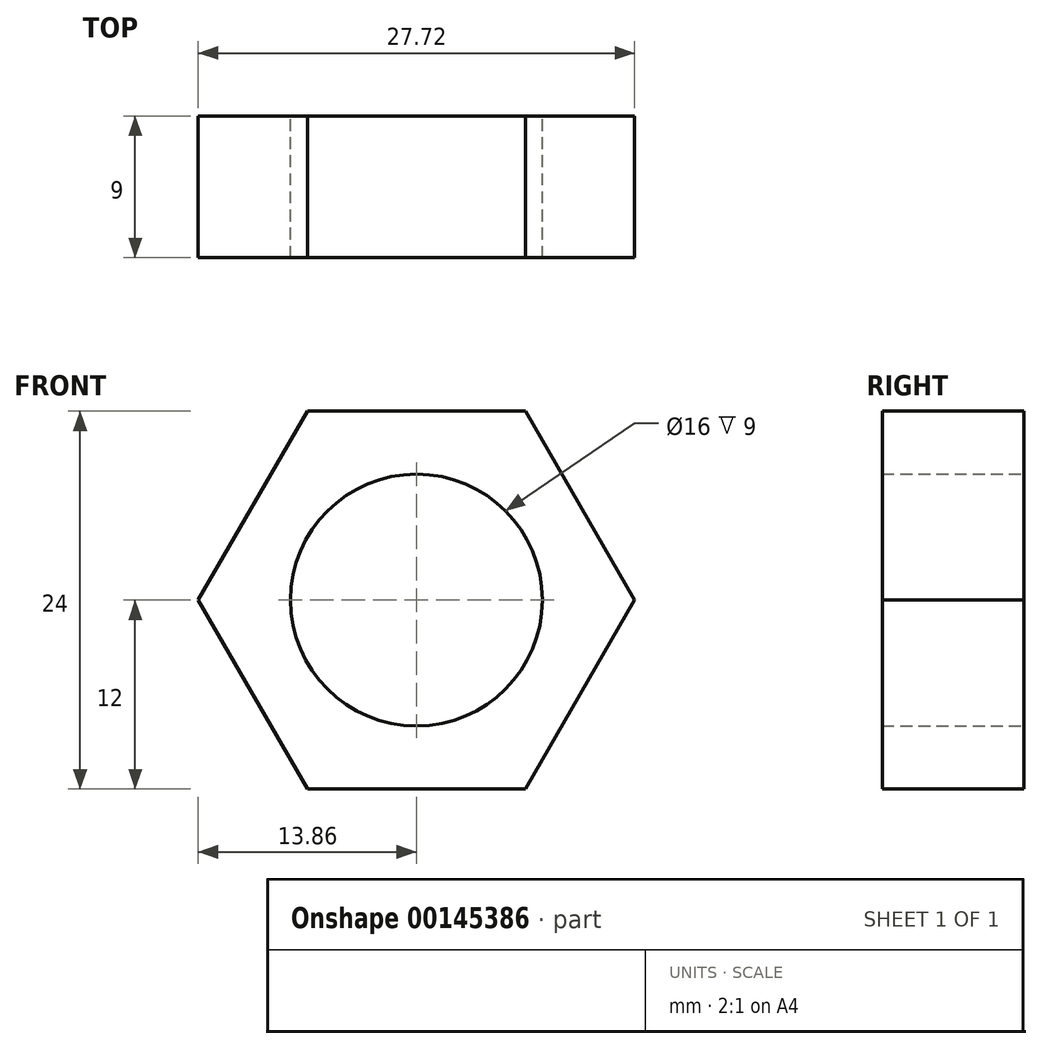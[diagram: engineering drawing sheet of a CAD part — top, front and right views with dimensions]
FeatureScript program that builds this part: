
annotation { "Feature Type Name" : "Feature", "Feature Type Description" : "" }
export const myFeature = defineFeature(function(context is Context, id is Id, definition is map)
    precondition{}
    {
        {
            var Q0;
            Q0=qCreatedBy(makeId("Front.planeOp"),FACE);
            var sketch = newSketch(context, id + "F0", { "sketchPlane" : qUnion([Q0])});
            skLineSegment(sketch, "E0", {"start": v(-17.83, 0) * mm, "end": v(24.73, 0) * mm, "construction": true});
            skLineSegment(sketch, "E1", {"start": v(-13.86, 0) * mm, "end": v(-6.93, 12) * mm});
            skLineSegment(sketch, "E2", {"start": v(-6.93, 12) * mm, "end": v(6.93, 12) * mm});
            skLineSegment(sketch, "E3", {"start": v(6.93, 12) * mm, "end": v(13.86, 0) * mm});
            skLineSegment(sketch, "E4", {"start": v(-13.86, 0) * mm, "end": v(-6.93, -12) * mm});
            skLineSegment(sketch, "E5", {"start": v(-6.93, -12) * mm, "end": v(6.93, -12) * mm});
            skLineSegment(sketch, "E6", {"start": v(6.93, -12) * mm, "end": v(13.86, 0) * mm});
            skLineSegment(sketch, "E7", {"start": v(0, 38.05) * mm, "end": v(0, -28.27) * mm, "construction": true});
            skPoint(sketch, "E7.endSnap0", {"position": v(0, 12) * mm});
            skCircle(sketch, "E8", {"center": v(0, 0) * mm, "radius": 8 * mm});
            skSolve(sketch);
        }
        {
            var Q0;
            Q0=qSketchRegion(id+"F0",true);
            extrude(context, id + "F1", {"entities" : qUnion([Q0]), "depth" : 9 * mm});
        }
    });
